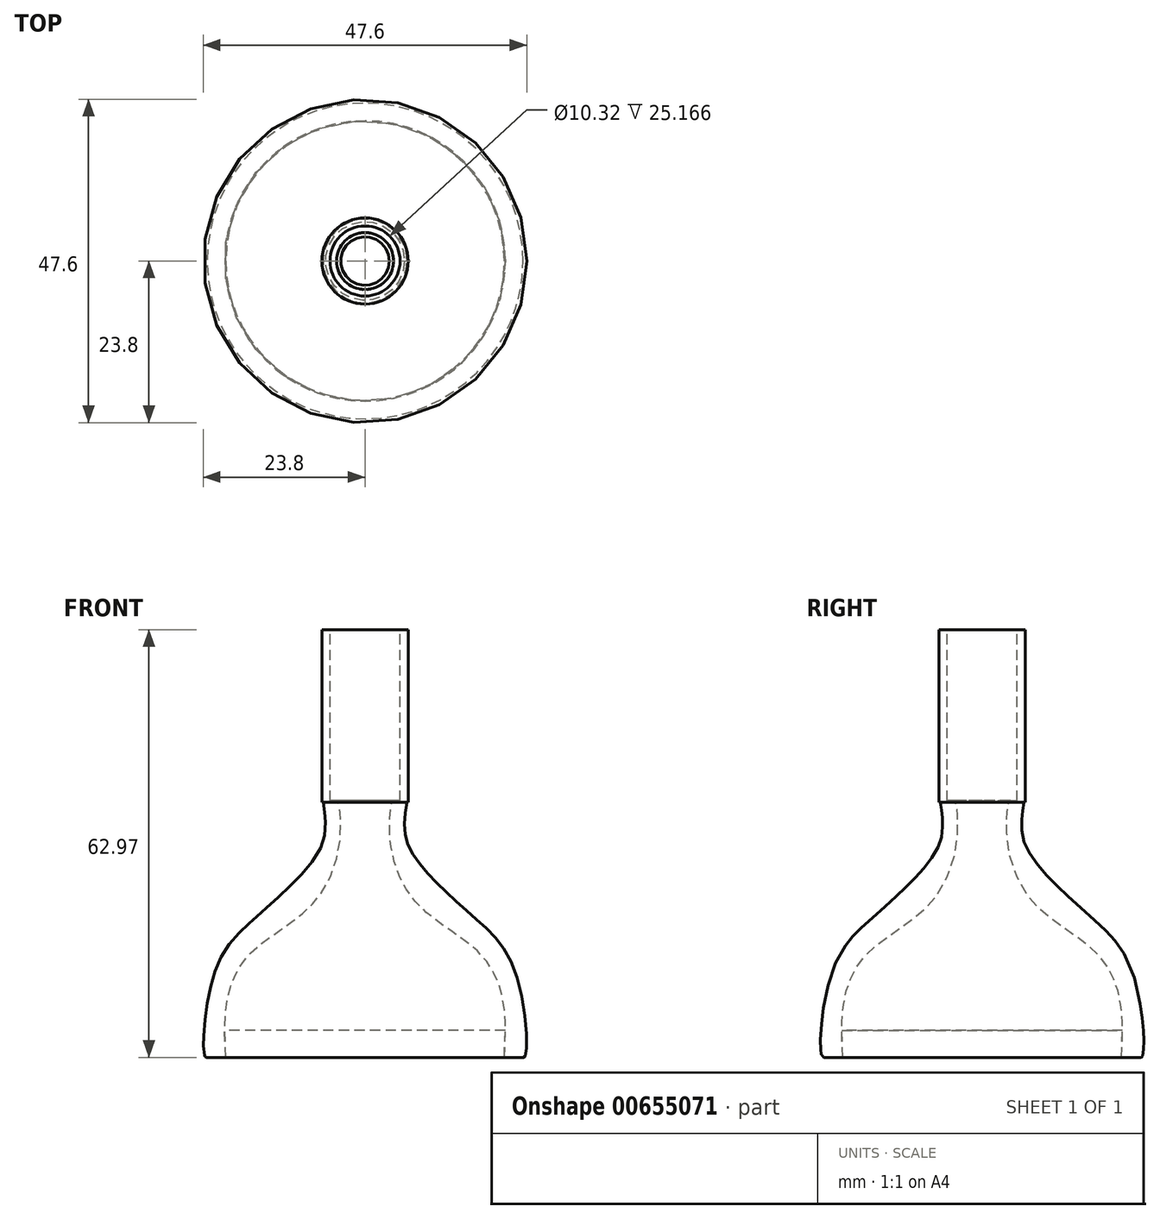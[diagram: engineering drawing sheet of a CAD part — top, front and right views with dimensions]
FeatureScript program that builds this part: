
annotation { "Feature Type Name" : "Feature", "Feature Type Description" : "" }
export const myFeature = defineFeature(function(context is Context, id is Id, definition is map)
    precondition{}
    {
        {
            var Q0;
            Q0=qCreatedBy(makeId("Top.planeOp"),FACE);
            var sketch = newSketch(context, id + "F0", { "sketchPlane" : qUnion([Q0])});
            skCircle(sketch, "E0", {"center": v(0, 0) * mm, "radius": 6.35 * mm});
            skCircle(sketch, "E1", {"center": v(0, 0) * mm, "radius": 5.16 * mm});
            skSolve(sketch);
        }
        {
            var Q0;
            Q0=makeQuery(id+"F0.imprint","IMPRINT",FACE,{"disambiguationData":[TD([[makeQuery(id+"F0.imprint","IMPRINT",EDGE,{"derivedFrom":sQuery(id+"F0.wireOp",EDGE,"E0")}),1.0]])]});
            extrude(context, id + "F1", {"entities" : qUnion([Q0]), "oppositeDirection" : true, "depth" : 25.4 * mm, "offsetDistance" : 25.4 * mm});
        }
        {
            var Q0;
            Q0=qCreatedBy(makeId("Front.planeOp"),FACE);
            var sketch = newSketch(context, id + "F2", { "sketchPlane" : qUnion([Q0])});
            skFitSpline(sketch, "E2", {"points": [v(-6.18, -25.2) * mm, v(-6.08, -30.9) * mm, v(-9.78, -36.45) * mm, v(-16.37, -42.63) * mm, v(-22.14, -50.46) * mm, v(-23.58, -62.81) * mm, v(-23.24, -62.97) * mm], "startDerivative": vector(5.67, -37.2) * mm, "endDerivative": vector(9.32, 0.67) * mm});
            skLineSegment(sketch, "E3", {"start": v(-23.24, -62.97) * mm, "end": v(-20.5, -62.97) * mm});
            skFitSpline(sketch, "E4", {"points": [v(-20.5, -62.97) * mm, v(-20.5, -55.81) * mm, v(-17.2, -47.99) * mm, v(-7.52, -40.16) * mm, v(-3.6, -29.86) * mm, v(-4.08, -25.15) * mm, v(-4.18, -25.15) * mm, v(-4.2, -25.13) * mm], "startDerivative": vector(-2.54, 39.61) * mm, "endDerivative": vector(-0.37, 2.55) * mm});
            skLineSegment(sketch, "E5", {"start": v(-4.2, -25.13) * mm, "end": v(-6.18, -25.2) * mm});
            skLineSegment(sketch, "E6", {"start": v(0, -14.89) * mm, "end": v(0, -15.76) * mm});
            skLineSegment(sketch, "E7", {"start": v(0, -24.31) * mm, "end": v(0, -57.3) * mm});
            skLineSegment(sketch, "E8", {"start": v(-20.5, -62.97) * mm, "end": v(0, -62.97) * mm});
            skLineSegment(sketch, "E9", {"start": v(0, -62.97) * mm, "end": v(0, -59) * mm});
            skLineSegment(sketch, "E10", {"start": v(0, -59) * mm, "end": v(-20.64, -59) * mm});
            skLineSegment(sketch, "E11", {"start": v(-20.64, -59) * mm, "end": v(-20.5, -62.97) * mm});
            skSolve(sketch);
        }
        {
            var Q0;
            Q0=makeQuery(id+"F2.imprint","IMPRINT",FACE,{"disambiguationData":[TD([[makeQuery(id+"F2.imprint","IMPRINT",EDGE,{"derivedFrom":sQuery(id+"F2.wireOp",EDGE,"E2")}),1.0]])]});
            var Q1;
            Q1=sQuery(id+"F2.wireOp",EDGE,"E7");
            revolve(context, id + "F3", {"operationType" : NewBodyOperationType.ADD, "entities" : qUnion([Q0]), "axis" : qUnion([Q1]), "revolveType" : RevolveType.FULL});
        }
        {
            var Q0;
            Q0=makeQuery(id+"F2.imprint","IMPRINT",FACE,{"disambiguationData":[TD([[makeQuery(id+"F2.imprint","IMPRINT",EDGE,{"derivedFrom":sQuery(id+"F2.wireOp",EDGE,"E8")}),1.0]])]});
            var Q1;
            Q1=sQuery(id+"F2.wireOp",EDGE,"E7");
            revolve(context, id + "F4", {"entities" : qUnion([Q0]), "axis" : qUnion([Q1]), "revolveType" : RevolveType.FULL});
        }
    });
